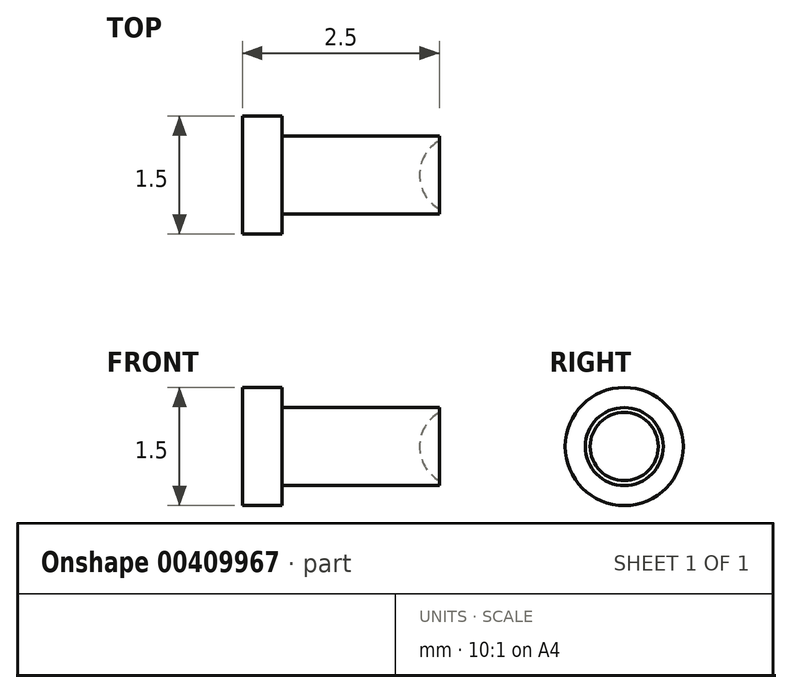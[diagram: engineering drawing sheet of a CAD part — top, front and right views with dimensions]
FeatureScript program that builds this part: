
annotation { "Feature Type Name" : "Feature", "Feature Type Description" : "" }
export const myFeature = defineFeature(function(context is Context, id is Id, definition is map)
    precondition{}
    {
        {
            var Q0;
            Q0=qCreatedBy(makeId("Right.planeOp"),FACE);
            var sketch = newSketch(context, id + "F0", { "sketchPlane" : qUnion([Q0])});
            skCircle(sketch, "E0", {"center": v(0, 0) * mm, "radius": 0.75 * mm});
            skCircle(sketch, "E1", {"center": v(0, 0) * mm, "radius": 0.5 * mm});
            skSolve(sketch);
        }
        {
            var Q0;
            Q0=makeQuery(id+"F0.imprint","IMPRINT",FACE,{"disambiguationData":[TD([[makeQuery(id+"F0.imprint","IMPRINT",EDGE,{"derivedFrom":sQuery(id+"F0.wireOp",EDGE,"E1")}),1.0]])]});
            extrude(context, id + "F1", {"entities" : qUnion([Q0]), "depth" : 2 * mm});
        }
        {
            var Q0;
            Q0 = qSketchRegion(id + "F0", true);
            var Q1;
            Q1=makeQuery(id+"F1.opExtrude","CAP_FACE",FACE,{"disambiguationData":[OSD([sQuery(id+"F0.wireOp",EDGE,"E1")])],"isStart":true});
            extrude(context, id + "F2", {"entities" : qUnion([Q0, Q1]), "operationType" : NewBodyOperationType.ADD, "depth" : -0.5 * mm});
        }
        {
            var Q0;
            Q0=qCreatedBy(makeId("Top.planeOp"),FACE);
            var sketch = newSketch(context, id + "F3", { "sketchPlane" : qUnion([Q0])});
            skLineSegment(sketch, "E2", {"start": v(0, 0) * mm, "end": v(3.17, 0) * mm, "construction": true});
            skArc(sketch, "E3", {"start": v(2.25, 0.5) * mm, "mid": v(1.75, 0) * mm, "end": v(2.25, -0.5) * mm});
            skLineSegment(sketch, "E4", {"start": v(2.25, 1) * mm, "end": v(2.25, -0.9) * mm, "construction": true});
            skLineSegment(sketch, "E5", {"start": v(2.25, 0.5) * mm, "end": v(2.25, -0.5) * mm});
            skSolve(sketch);
        }
        {
            var Q0;
            Q0 = qSketchRegion(id + "F3", true);
            var Q1;
            Q1=sQuery(id+"F3.wireOp",EDGE,"E4");
            revolve(context, id + "F4", {"operationType" : NewBodyOperationType.REMOVE, "entities" : qUnion([Q0]), "axis" : qUnion([Q1]), "revolveType" : RevolveType.FULL, "oppositeDirection" : true});
        }
    });
